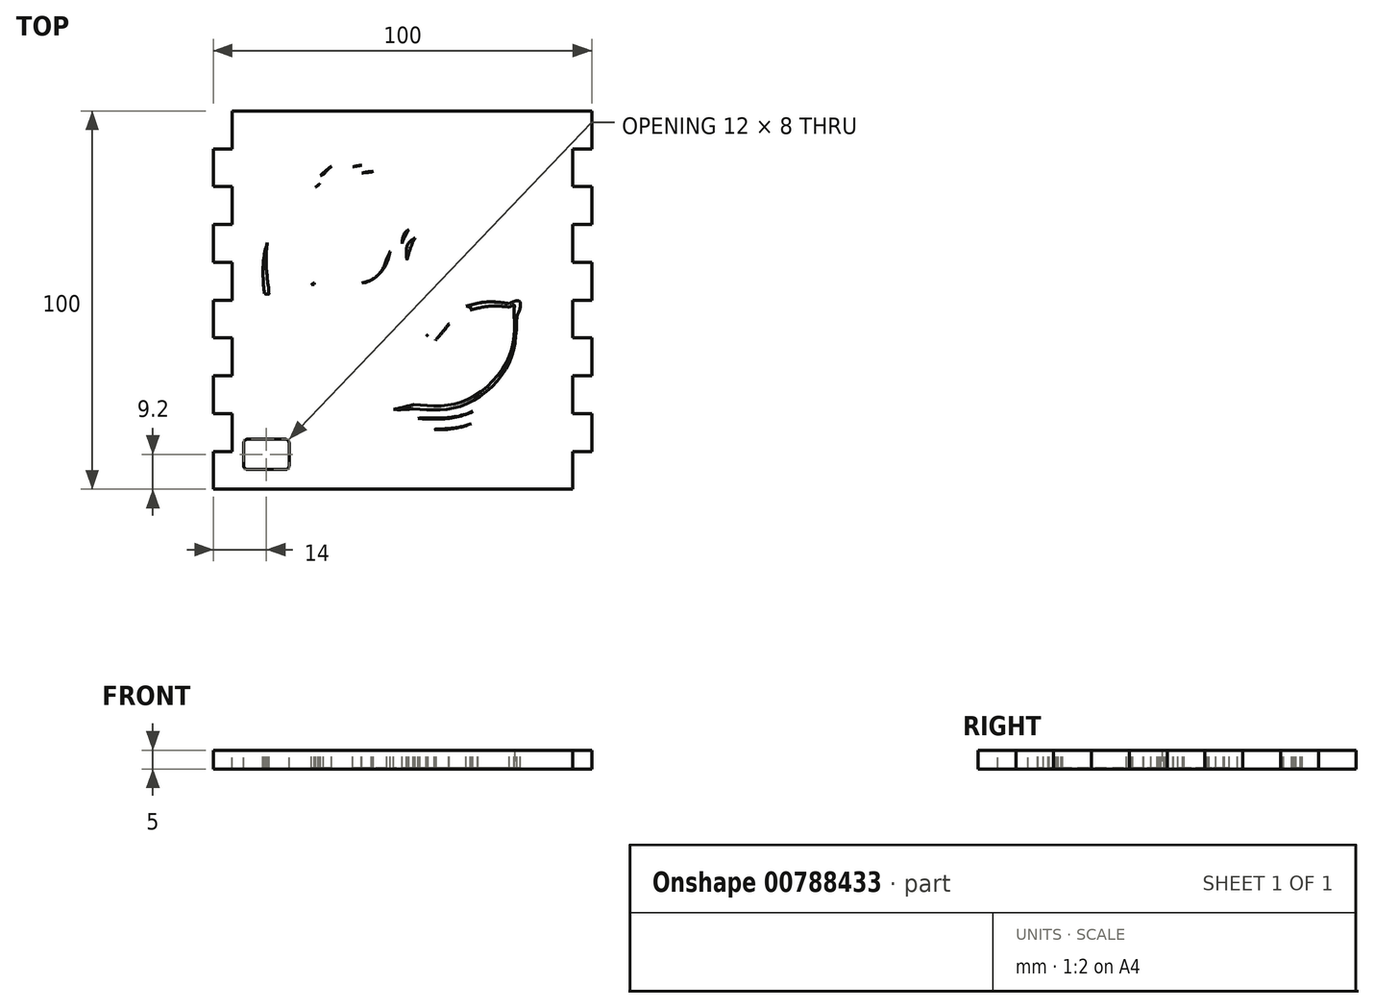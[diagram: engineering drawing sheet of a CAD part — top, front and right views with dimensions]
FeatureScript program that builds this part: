
annotation { "Feature Type Name" : "Feature", "Feature Type Description" : "" }
export const myFeature = defineFeature(function(context is Context, id is Id, definition is map)
    precondition{}
    {
        {
            var Q0;
            Q0=qCreatedBy(makeId("Top.planeOp"),FACE);
            var sketch = newSketch(context, id + "F0", { "sketchPlane" : qUnion([Q0])});
            skLineSegment(sketch, "E0.bottom", {"start": v(50, -50) * mm, "end": v(-50, -50) * mm});
            skLineSegment(sketch, "E0.top", {"start": v(50, 50) * mm, "end": v(-50, 50) * mm});
            skLineSegment(sketch, "E0.left", {"start": v(50, -50) * mm, "end": v(50, 50) * mm});
            skLineSegment(sketch, "E0.right", {"start": v(-50, -50) * mm, "end": v(-50, 50) * mm});
            skPoint(sketch, "E0.middle", {"position": v(0, 0) * mm});
            skSolve(sketch);
        }
        {
            var Q0;
            Q0=qSketchRegion(id+"F0",true);
            extrude(context, id + "F1", {"entities" : qUnion([Q0]), "depth" : 5 * mm, "offsetDistance" : 25 * mm});
        }
        {
            var Q0;
            Q0=makeQuery(id+"F1.opExtrude","CAP_FACE",FACE,{"disambiguationData":[OSD([sQuery(id+"F0.wireOp",EDGE,"E0.bottom"),sQuery(id+"F0.wireOp",EDGE,"E0.top"),sQuery(id+"F0.wireOp",EDGE,"E0.left"),sQuery(id+"F0.wireOp",EDGE,"E0.right")])],"isStart":false});
            var sketch = newSketch(context, id + "F2", { "sketchPlane" : qUnion([Q0])});
            skLineSegment(sketch, "E1.bottom", {"start": v(-50, 50) * mm, "end": v(-45, 50) * mm});
            skLineSegment(sketch, "E1.top", {"start": v(-50, 40) * mm, "end": v(-45, 40) * mm});
            skLineSegment(sketch, "E1.left", {"start": v(-50, 50) * mm, "end": v(-50, 40) * mm});
            skLineSegment(sketch, "E1.right", {"start": v(-45, 50) * mm, "end": v(-45, 40) * mm});
            skLineSegment(sketch, "E2.bottom", {"start": v(-45, 30) * mm, "end": v(-55, 30) * mm});
            skLineSegment(sketch, "E2.top", {"start": v(-45, 20) * mm, "end": v(-55, 20) * mm});
            skLineSegment(sketch, "E2.left", {"start": v(-45, 30) * mm, "end": v(-45, 20) * mm});
            skLineSegment(sketch, "E2.right", {"start": v(-55, 30) * mm, "end": v(-55, 20) * mm});
            skLineSegment(sketch, "E3.bottom", {"start": v(-45, 10) * mm, "end": v(-55, 10) * mm});
            skLineSegment(sketch, "E3.top", {"start": v(-45, 0) * mm, "end": v(-55, 0) * mm});
            skLineSegment(sketch, "E3.left", {"start": v(-45, 10) * mm, "end": v(-45, 0) * mm});
            skLineSegment(sketch, "E3.right", {"start": v(-55, 10) * mm, "end": v(-55, 0) * mm});
            skLineSegment(sketch, "E4.bottom", {"start": v(-45, -10) * mm, "end": v(-55, -10) * mm});
            skLineSegment(sketch, "E4.top", {"start": v(-45, -20) * mm, "end": v(-55, -20) * mm});
            skLineSegment(sketch, "E4.left", {"start": v(-45, -10) * mm, "end": v(-45, -20) * mm});
            skLineSegment(sketch, "E4.right", {"start": v(-55, -10) * mm, "end": v(-55, -20) * mm});
            skLineSegment(sketch, "E5.bottom", {"start": v(-55, -30) * mm, "end": v(-45, -30) * mm});
            skLineSegment(sketch, "E5.top", {"start": v(-55, -40) * mm, "end": v(-45, -40) * mm});
            skLineSegment(sketch, "E5.left", {"start": v(-55, -30) * mm, "end": v(-55, -40) * mm});
            skLineSegment(sketch, "E5.right", {"start": v(-45, -30) * mm, "end": v(-45, -40) * mm});
            skSolve(sketch);
        }
        {
            var Q0;
            Q0=qSketchRegion(id+"F2",true);
            extrude(context, id + "F3", {"entities" : qUnion([Q0]), "operationType" : NewBodyOperationType.REMOVE, "oppositeDirection" : true, "depth" : 5 * mm, "offsetDistance" : 25 * mm});
        }
        {
            var Q0;
            Q0=makeQuery(id+"F1.opExtrude","CAP_FACE",FACE,{"disambiguationData":[OSD([sQuery(id+"F0.wireOp",EDGE,"E0.bottom"),sQuery(id+"F0.wireOp",EDGE,"E0.top"),sQuery(id+"F0.wireOp",EDGE,"E0.left"),sQuery(id+"F0.wireOp",EDGE,"E0.right")])],"isStart":false});
            var sketch = newSketch(context, id + "F4", { "sketchPlane" : qUnion([Q0])});
            skLineSegment(sketch, "E6.bottom", {"start": v(45, -40) * mm, "end": v(50, -40) * mm});
            skLineSegment(sketch, "E6.top", {"start": v(45, -50) * mm, "end": v(50, -50) * mm});
            skLineSegment(sketch, "E6.left", {"start": v(45, -40) * mm, "end": v(45, -50) * mm});
            skLineSegment(sketch, "E6.right", {"start": v(50, -40) * mm, "end": v(50, -50) * mm});
            skLineSegment(sketch, "E7.bottom", {"start": v(45, -20) * mm, "end": v(50, -20) * mm});
            skLineSegment(sketch, "E7.top", {"start": v(45, -30) * mm, "end": v(50, -30) * mm});
            skLineSegment(sketch, "E7.left", {"start": v(45, -20) * mm, "end": v(45, -30) * mm});
            skLineSegment(sketch, "E7.right", {"start": v(50, -20) * mm, "end": v(50, -30) * mm});
            skLineSegment(sketch, "E8.bottom", {"start": v(45, 0) * mm, "end": v(50, 0) * mm});
            skLineSegment(sketch, "E8.top", {"start": v(45, -10) * mm, "end": v(50, -10) * mm});
            skLineSegment(sketch, "E8.left", {"start": v(45, 0) * mm, "end": v(45, -10) * mm});
            skLineSegment(sketch, "E8.right", {"start": v(50, 0) * mm, "end": v(50, -10) * mm});
            skLineSegment(sketch, "E9.bottom", {"start": v(45, 20) * mm, "end": v(50, 20) * mm});
            skLineSegment(sketch, "E9.top", {"start": v(45, 10) * mm, "end": v(50, 10) * mm});
            skLineSegment(sketch, "E9.left", {"start": v(45, 20) * mm, "end": v(45, 10) * mm});
            skLineSegment(sketch, "E9.right", {"start": v(50, 20) * mm, "end": v(50, 10) * mm});
            skLineSegment(sketch, "E10.bottom", {"start": v(45, 40) * mm, "end": v(50, 40) * mm});
            skLineSegment(sketch, "E10.top", {"start": v(45, 30) * mm, "end": v(50, 30) * mm});
            skLineSegment(sketch, "E10.left", {"start": v(45, 40) * mm, "end": v(45, 30) * mm});
            skLineSegment(sketch, "E10.right", {"start": v(50, 40) * mm, "end": v(50, 30) * mm});
            skSolve(sketch);
        }
        {
            var Q0;
            Q0=qSketchRegion(id+"F4",true);
            extrude(context, id + "F5", {"entities" : qUnion([Q0]), "operationType" : NewBodyOperationType.REMOVE, "oppositeDirection" : true, "depth" : 5 * mm, "offsetDistance" : 25 * mm});
        }
        {
            var Q0;
            Q0=makeQuery(id+"F1.opExtrude","CAP_FACE",FACE,{"disambiguationData":[OSD([sQuery(id+"F0.wireOp",EDGE,"E0.bottom"),sQuery(id+"F0.wireOp",EDGE,"E0.top"),sQuery(id+"F0.wireOp",EDGE,"E0.left"),sQuery(id+"F0.wireOp",EDGE,"E0.right")])],"isStart":false});
            var sketch = newSketch(context, id + "F6", { "sketchPlane" : qUnion([Q0])});
            skFitSpline(sketch, "E11", {"points": [v(-1.5, -35.05) * mm, v(-16.6, -34.56) * mm, v(-30.6, -23.77) * mm, v(-34.95, -9.31) * mm]});
            skFitSpline(sketch, "E12", {"points": [v(-34.95, -9.31) * mm, v(-39.38, 4.29) * mm, v(-34.95, 20.21) * mm, v(-24.04, 29.5) * mm]});
            skFitSpline(sketch, "E13", {"points": [v(-24.04, 29.5) * mm, v(-12.77, 39.67) * mm, v(4.96, 41.47) * mm, v(18.1, 33.94) * mm]});
            skFitSpline(sketch, "E14", {"points": [v(18.1, 33.94) * mm, v(30.56, 27.18) * mm, v(38.25, 12.78) * mm, v(36.9, -1.33) * mm]});
            skFitSpline(sketch, "E15", {"points": [v(36.9, -1.33) * mm, v(35.83, -16.44) * mm, v(24.45, -30.09) * mm, v(9.77, -33.82) * mm]});
            skFitSpline(sketch, "E16", {"points": [v(9.77, -33.82) * mm, v(6.1, -34.81) * mm, v(2.28, -35.24) * mm, v(-1.5, -35.05) * mm]});
            skFitSpline(sketch, "E17", {"points": [v(3.11, -34.85) * mm, v(18.23, -33.86) * mm, v(31.88, -22.48) * mm, v(35.63, -7.82) * mm]});
            skFitSpline(sketch, "E18", {"points": [v(35.63, -7.82) * mm, v(36.47, -4.77) * mm, v(36.85, -1.61) * mm, v(36.92, 1.55) * mm]});
            skFitSpline(sketch, "E19", {"points": [v(36.92, 1.55) * mm, v(34.37, 0.85) * mm, v(36.28, -4.46) * mm, v(34.77, -6.8) * mm]});
            skFitSpline(sketch, "E20", {"points": [v(34.77, -6.8) * mm, v(31.4, -21.33) * mm, v(18, -32.73) * mm, v(3.12, -33.75) * mm]});
            skFitSpline(sketch, "E21", {"points": [v(3.12, -33.75) * mm, v(-11.13, -35.13) * mm, v(-25.62, -26.87) * mm, v(-31.78, -13.97) * mm]});
            skFitSpline(sketch, "E22", {"points": [v(-31.78, -13.97) * mm, v(-34.01, -9.49) * mm, v(-35.2, -4.53) * mm, v(-35.42, 0.47) * mm]});
            skFitSpline(sketch, "E23", {"points": [v(-35.42, 0.47) * mm, v(-30.66, 0.48) * mm, v(-25.9, 0.48) * mm, v(-21.15, 0.5) * mm]});
            skFitSpline(sketch, "E24", {"points": [v(-21.15, 0.5) * mm, v(-21.52, 2.1) * mm, v(-23.24, 1.37) * mm, v(-24.46, 1.53) * mm]});
            skFitSpline(sketch, "E25", {"points": [v(-24.46, 1.53) * mm, v(-28.48, 1.53) * mm, v(-32.51, 1.54) * mm, v(-36.54, 1.55) * mm]});
            skFitSpline(sketch, "E26", {"points": [v(-36.54, 1.55) * mm, v(-36.6, -12.8) * mm, v(-27.4, -26.62) * mm, v(-14.12, -32.06) * mm]});
            skFitSpline(sketch, "E27", {"points": [v(-14.12, -32.06) * mm, v(-8.7, -34.37) * mm, v(-2.75, -35.3) * mm, v(3.11, -34.85) * mm]});
            skFitSpline(sketch, "E28", {"points": [v(1.99, -33.7) * mm, v(16.8, -33.17) * mm, v(30.44, -22.27) * mm, v(34.32, -7.98) * mm]});
            skFitSpline(sketch, "E29", {"points": [v(34.32, -7.98) * mm, v(35.22, -4.89) * mm, v(35.63, -1.67) * mm, v(35.7, 1.55) * mm]});
            skFitSpline(sketch, "E30", {"points": [v(35.7, 1.55) * mm, v(33.32, 0.9) * mm, v(34.96, -3.87) * mm, v(33.67, -6.14) * mm]});
            skFitSpline(sketch, "E31", {"points": [v(33.67, -6.14) * mm, v(30.57, -20.12) * mm, v(17.9, -31.27) * mm, v(3.61, -32.48) * mm]});
            skFitSpline(sketch, "E32", {"points": [v(3.61, -32.48) * mm, v(-10.39, -34.09) * mm, v(-24.77, -26.01) * mm, v(-30.76, -13.27) * mm]});
            skFitSpline(sketch, "E33", {"points": [v(-30.76, -13.27) * mm, v(-32.66, -9.36) * mm, v(-33.81, -5.09) * mm, v(-34.11, -0.75) * mm]});
            skFitSpline(sketch, "E34", {"points": [v(-34.11, -0.75) * mm, v(-29.54, -0.74) * mm, v(-24.98, -0.74) * mm, v(-20.4, -0.73) * mm]});
            skFitSpline(sketch, "E35", {"points": [v(-20.4, -0.73) * mm, v(-20.82, 0.86) * mm, v(-22.52, 0.16) * mm, v(-23.75, 0.3) * mm]});
            skFitSpline(sketch, "E36", {"points": [v(-23.75, 0.3) * mm, v(-27.6, 0.31) * mm, v(-31.44, 0.32) * mm, v(-35.28, 0.33) * mm]});
            skFitSpline(sketch, "E37", {"points": [v(-35.28, 0.33) * mm, v(-34.9, -14.29) * mm, v(-24.47, -27.89) * mm, v(-10.48, -32.1) * mm]});
            skFitSpline(sketch, "E38", {"points": [v(-10.48, -32.1) * mm, v(-6.47, -33.38) * mm, v(-2.22, -33.9) * mm, v(1.99, -33.7) * mm]});
            skFitSpline(sketch, "E39", {"points": [v(1.94, -32.48) * mm, v(15.86, -31.96) * mm, v(28.76, -22) * mm, v(32.83, -8.69) * mm]});
            skFitSpline(sketch, "E40", {"points": [v(32.83, -8.69) * mm, v(33.9, -5.38) * mm, v(34.42, -1.92) * mm, v(34.46, 1.55) * mm]});
            skFitSpline(sketch, "E41", {"points": [v(34.46, 1.55) * mm, v(31.93, 1.7) * mm, v(33.96, -2.9) * mm, v(32.78, -4.52) * mm]});
            skFitSpline(sketch, "E42", {"points": [v(32.78, -4.52) * mm, v(30.31, -18.23) * mm, v(18.38, -29.53) * mm, v(4.53, -31.14) * mm]});
            skFitSpline(sketch, "E43", {"points": [v(4.53, -31.14) * mm, v(-8.56, -33.06) * mm, v(-22.3, -26.17) * mm, v(-28.68, -14.6) * mm]});
            skFitSpline(sketch, "E44", {"points": [v(-28.68, -14.6) * mm, v(-30.89, -10.73) * mm, v(-32.28, -6.41) * mm, v(-32.79, -2) * mm]});
            skFitSpline(sketch, "E45", {"points": [v(-32.79, -2) * mm, v(-28.4, -1.95) * mm, v(-24, -1.96) * mm, v(-19.62, -1.95) * mm]});
            skFitSpline(sketch, "E46", {"points": [v(-19.62, -1.95) * mm, v(-20, -0.5) * mm, v(-21.43, -0.93) * mm, v(-22.6, -0.9) * mm]});
            skFitSpline(sketch, "E47", {"points": [v(-22.6, -0.9) * mm, v(-26.4, -0.9) * mm, v(-30.2, -0.9) * mm, v(-33.99, -0.9) * mm]});
            skFitSpline(sketch, "E48", {"points": [v(-33.99, -0.9) * mm, v(-33.08, -14.98) * mm, v(-22.54, -27.74) * mm, v(-8.88, -31.3) * mm]});
            skFitSpline(sketch, "E49", {"points": [v(-8.88, -31.3) * mm, v(-5.37, -32.27) * mm, v(-1.7, -32.65) * mm, v(1.94, -32.48) * mm]});
            skFitSpline(sketch, "E50", {"points": [v(2.93, -31.19) * mm, v(16.67, -30.25) * mm, v(29.04, -19.74) * mm, v(32.23, -6.35) * mm]});
            skFitSpline(sketch, "E51", {"points": [v(32.23, -6.35) * mm, v(32.9, -3.77) * mm, v(33.2, -1.11) * mm, v(33.25, 1.55) * mm]});
            skFitSpline(sketch, "E52", {"points": [v(33.25, 1.55) * mm, v(26.5, 1.68) * mm, v(19.7, 1.12) * mm, v(13, 2.13) * mm]});
            skFitSpline(sketch, "E53", {"points": [v(13, 2.13) * mm, v(8.36, 2.87) * mm, v(4.32, 5.96) * mm, v(2.22, 10.13) * mm]});
            skFitSpline(sketch, "E54", {"points": [v(2.22, 10.13) * mm, v(1.4, 6.17) * mm, v(6.94, 2.99) * mm, v(10.39, 1.69) * mm]});
            skFitSpline(sketch, "E55", {"points": [v(10.39, 1.69) * mm, v(16.73, -0.21) * mm, v(23.42, 0.69) * mm, v(29.95, 0.47) * mm]});
            skFitSpline(sketch, "E56", {"points": [v(29.95, 0.47) * mm, v(33.12, 1.41) * mm, v(32.02, -1.75) * mm, v(31.65, -3.85) * mm]});
            skFitSpline(sketch, "E57", {"points": [v(31.65, -3.85) * mm, v(29.45, -17.51) * mm, v(17.4, -28.76) * mm, v(3.63, -30.02) * mm]});
            skFitSpline(sketch, "E58", {"points": [v(3.63, -30.02) * mm, v(-9.54, -31.64) * mm, v(-23.17, -24.02) * mm, v(-28.68, -11.94) * mm]});
            skFitSpline(sketch, "E59", {"points": [v(-28.68, -11.94) * mm, v(-30.7, -9.2) * mm, v(-30.39, -4.2) * mm, v(-32.1, -2.11) * mm]});
            skFitSpline(sketch, "E60", {"points": [v(-32.1, -2.11) * mm, v(-33.32, -4.07) * mm, v(-30.97, -8.8) * mm, v(-30.11, -11.46) * mm]});
            skFitSpline(sketch, "E61", {"points": [v(-30.11, -11.46) * mm, v(-24.71, -24.22) * mm, v(-10.89, -32.5) * mm, v(2.93, -31.19) * mm]});
            skFitSpline(sketch, "E62", {"points": [v(1.8, -30.03) * mm, v(15.26, -29.56) * mm, v(27.63, -19.54) * mm, v(30.94, -6.49) * mm]});
            skFitSpline(sketch, "E63", {"points": [v(30.94, -6.49) * mm, v(30.84, -4.7) * mm, v(33.53, 0.22) * mm, v(30.95, 0.32) * mm]});
            skFitSpline(sketch, "E64", {"points": [v(30.95, 0.32) * mm, v(24.5, 0.51) * mm, v(17.97, -0.2) * mm, v(11.63, 1.19) * mm]});
            skFitSpline(sketch, "E65", {"points": [v(11.63, 1.19) * mm, v(7.38, 2.14) * mm, v(3.78, 5.04) * mm, v(1.56, 8.74) * mm]});
            skFitSpline(sketch, "E66", {"points": [v(1.56, 8.74) * mm, v(0.56, 5.95) * mm, v(4.6, 3.6) * mm, v(6.7, 2.01) * mm]});
            skFitSpline(sketch, "E67", {"points": [v(6.7, 2.01) * mm, v(13.32, -1.76) * mm, v(21.17, -0.5) * mm, v(28.46, -0.75) * mm]});
            skFitSpline(sketch, "E68", {"points": [v(28.46, -0.75) * mm, v(31, -0.1) * mm, v(31.25, -1.65) * mm, v(30.4, -3.9) * mm]});
            skFitSpline(sketch, "E69", {"points": [v(30.4, -3.9) * mm, v(28.11, -17.42) * mm, v(15.8, -28.33) * mm, v(2.1, -28.92) * mm]});
            skFitSpline(sketch, "E70", {"points": [v(2.1, -28.92) * mm, v(-11.15, -29.95) * mm, v(-24.37, -21.3) * mm, v(-28.71, -8.74) * mm]});
            skFitSpline(sketch, "E71", {"points": [v(-28.71, -8.74) * mm, v(-30.23, -7.25) * mm, v(-28.96, -1.48) * mm, v(-31.4, -2.27) * mm]});
            skFitSpline(sketch, "E72", {"points": [v(-31.4, -2.27) * mm, v(-29.89, -15.47) * mm, v(-19.25, -26.96) * mm, v(-6.19, -29.43) * mm]});
            skFitSpline(sketch, "E73", {"points": [v(-6.19, -29.43) * mm, v(-3.57, -29.97) * mm, v(-0.87, -30.18) * mm, v(1.8, -30.03) * mm]});
            skFitSpline(sketch, "E74", {"points": [v(2.83, -28.75) * mm, v(16.07, -27.8) * mm, v(27.83, -17.26) * mm, v(30.21, -4.21) * mm]});
            skFitSpline(sketch, "E75", {"points": [v(30.21, -4.21) * mm, v(31.14, -1.82) * mm, v(30.83, -0.24) * mm, v(28.17, -0.9) * mm]});
            skFitSpline(sketch, "E76", {"points": [v(28.17, -0.9) * mm, v(20.7, -0.66) * mm, v(12.58, -1.92) * mm, v(5.96, 2.32) * mm]});
            skFitSpline(sketch, "E77", {"points": [v(5.96, 2.32) * mm, v(3.8, 3.18) * mm, v(2.04, 6.74) * mm, v(0.7, 7.24) * mm]});
            skFitSpline(sketch, "E78", {"points": [v(0.7, 7.24) * mm, v(0, 4.46) * mm, v(4.79, 2.06) * mm, v(6.83, 0.55) * mm]});
            skFitSpline(sketch, "E79", {"points": [v(6.83, 0.55) * mm, v(13.85, -2.97) * mm, v(21.86, -1.75) * mm, v(29.44, -1.97) * mm]});
            skFitSpline(sketch, "E80", {"points": [v(29.44, -1.97) * mm, v(28.04, -15.33) * mm, v(16.32, -26.65) * mm, v(2.92, -27.64) * mm]});
            skFitSpline(sketch, "E81", {"points": [v(2.92, -27.64) * mm, v(-9.73, -29.02) * mm, v(-22.62, -21.13) * mm, v(-27.2, -9.26) * mm]});
            skFitSpline(sketch, "E82", {"points": [v(-27.2, -9.26) * mm, v(-28.51, -7.6) * mm, v(-28.38, -1.31) * mm, v(-30.12, -2.55) * mm]});
            skFitSpline(sketch, "E83", {"points": [v(-30.12, -2.55) * mm, v(-28.49, -15.41) * mm, v(-17.8, -26.42) * mm, v(-4.98, -28.42) * mm]});
            skFitSpline(sketch, "E84", {"points": [v(-4.98, -28.42) * mm, v(-2.4, -28.88) * mm, v(0.22, -28.93) * mm, v(2.83, -28.75) * mm]});
            skFitSpline(sketch, "E85", {"points": [v(2.74, -27.53) * mm, v(15.84, -26.6) * mm, v(27.4, -15.85) * mm, v(29.22, -2.83) * mm]});
            skFitSpline(sketch, "E86", {"points": [v(29.22, -2.83) * mm, v(29.53, -1.36) * mm, v(26.82, -2.45) * mm, v(25.8, -2.11) * mm]});
            skFitSpline(sketch, "E87", {"points": [v(25.8, -2.11) * mm, v(23.82, -2.11) * mm, v(21.85, -2.11) * mm, v(19.89, -2.11) * mm]});
            skFitSpline(sketch, "E88", {"points": [v(19.89, -2.11) * mm, v(14.22, -10.41) * mm, v(7.3, -17.76) * mm, v(0.17, -24.81) * mm]});
            skFitSpline(sketch, "E89", {"points": [v(0.17, -24.81) * mm, v(-6.95, -17.76) * mm, v(-13.85, -10.4) * mm, v(-19.52, -2.11) * mm]});
            skFitSpline(sketch, "E90", {"points": [v(-19.52, -2.11) * mm, v(-22.66, -2.15) * mm, v(-25.8, -2.03) * mm, v(-28.94, -2.2) * mm]});
            skFitSpline(sketch, "E91", {"points": [v(-28.94, -2.2) * mm, v(-27.41, -14.94) * mm, v(-16.6, -25.81) * mm, v(-3.85, -27.36) * mm]});
            skFitSpline(sketch, "E92", {"points": [v(-3.85, -27.36) * mm, v(-1.67, -27.69) * mm, v(0.54, -27.67) * mm, v(2.74, -27.53) * mm]});
            skFitSpline(sketch, "E93", {"points": [v(2.16, -22.65) * mm, v(8.51, -16.27) * mm, v(14.61, -9.56) * mm, v(19.73, -2.12) * mm]});
            skFitSpline(sketch, "E94", {"points": [v(19.73, -2.12) * mm, v(17.02, -2.08) * mm, v(16.34, -5.94) * mm, v(14.4, -7.5) * mm]});
            skFitSpline(sketch, "E95", {"points": [v(14.4, -7.5) * mm, v(9.99, -13) * mm, v(5.16, -18.15) * mm, v(0.16, -23.11) * mm]});
            skFitSpline(sketch, "E96", {"points": [v(0.16, -23.11) * mm, v(-7.9, -14.85) * mm, v(-16.14, -6.42) * mm, v(-21.58, 3.87) * mm]});
            skFitSpline(sketch, "E97", {"points": [v(-21.58, 3.87) * mm, v(-25.9, 11.84) * mm, v(-19.67, 22.3) * mm, v(-11.03, 23.6) * mm]});
            skFitSpline(sketch, "E98", {"points": [v(-11.03, 23.6) * mm, v(-7.25, 24.28) * mm, v(-3.29, 22.83) * mm, v(-0.65, 20.08) * mm]});
            skFitSpline(sketch, "E99", {"points": [v(-0.65, 20.08) * mm, v(0.72, 22.26) * mm, v(-4.23, 23.8) * mm, v(-6.06, 24.47) * mm]});
            skFitSpline(sketch, "E100", {"points": [v(-6.06, 24.47) * mm, v(-15.9, 27) * mm, v(-25.96, 16.75) * mm, v(-23.8, 6.95) * mm]});
            skFitSpline(sketch, "E101", {"points": [v(-23.8, 6.95) * mm, v(-22.04, 0.56) * mm, v(-17.6, -4.64) * mm, v(-13.6, -9.77) * mm]});
            skFitSpline(sketch, "E102", {"points": [v(-13.6, -9.77) * mm, v(-9.3, -14.99) * mm, v(-4.65, -19.9) * mm, v(0.16, -24.64) * mm]});
            skFitSpline(sketch, "E103", {"points": [v(0.16, -24.64) * mm, v(0.84, -23.99) * mm, v(1.5, -23.32) * mm, v(2.16, -22.65) * mm]});
            skFitSpline(sketch, "E104", {"points": [v(1.92, -21.15) * mm, v(7.82, -15.2) * mm, v(13.46, -8.96) * mm, v(18.26, -2.09) * mm]});
            skFitSpline(sketch, "E105", {"points": [v(18.26, -2.09) * mm, v(15.47, -1.69) * mm, v(14.94, -6.02) * mm, v(12.91, -7.39) * mm]});
            skFitSpline(sketch, "E106", {"points": [v(12.91, -7.39) * mm, v(8.93, -12.3) * mm, v(4.63, -16.93) * mm, v(0.16, -21.38) * mm]});
            skFitSpline(sketch, "E107", {"points": [v(0.16, -21.38) * mm, v(-7.46, -13.55) * mm, v(-15.16, -5.5) * mm, v(-20.38, 4.19) * mm]});
            skFitSpline(sketch, "E108", {"points": [v(-20.38, 4.19) * mm, v(-24.4, 11.3) * mm, v(-19.1, 20.73) * mm, v(-11.42, 22.29) * mm]});
            skFitSpline(sketch, "E109", {"points": [v(-11.42, 22.29) * mm, v(-7.64, 23.75) * mm, v(-3.54, 20.52) * mm, v(-1.07, 19.57) * mm]});
            skFitSpline(sketch, "E110", {"points": [v(-1.07, 19.57) * mm, v(-1.43, 22.24) * mm, v(-6.84, 23.8) * mm, v(-9.66, 23.62) * mm]});
            skFitSpline(sketch, "E111", {"points": [v(-9.66, 23.62) * mm, v(-18.56, 23.27) * mm, v(-25.63, 12.93) * mm, v(-21.8, 4.64) * mm]});
            skFitSpline(sketch, "E112", {"points": [v(-21.8, 4.64) * mm, v(-17.22, -4.66) * mm, v(-10, -12.3) * mm, v(-2.95, -19.77) * mm]});
            skFitSpline(sketch, "E113", {"points": [v(-2.95, -19.77) * mm, v(-1.13, -21.16) * mm, v(0.03, -24.64) * mm, v(1.92, -21.15) * mm]});
            skFitSpline(sketch, "E114", {"points": [v(1.73, -19.6) * mm, v(7.15, -14.1) * mm, v(12.32, -8.33) * mm, v(16.82, -2.04) * mm]});
            skFitSpline(sketch, "E115", {"points": [v(16.82, -2.04) * mm, v(14.41, -1.4) * mm, v(13.95, -5.13) * mm, v(12.27, -6.25) * mm]});
            skFitSpline(sketch, "E116", {"points": [v(12.27, -6.25) * mm, v(8.48, -10.93) * mm, v(4.42, -15.39) * mm, v(0.16, -19.64) * mm]});
            skFitSpline(sketch, "E117", {"points": [v(0.16, -19.64) * mm, v(-7.1, -12.08) * mm, v(-14.52, -4.35) * mm, v(-19.42, 5.01) * mm]});
            skFitSpline(sketch, "E118", {"points": [v(-19.42, 5.01) * mm, v(-23.53, 12.64) * mm, v(-15.69, 22.8) * mm, v(-7.32, 21.13) * mm]});
            skFitSpline(sketch, "E119", {"points": [v(-7.32, 21.13) * mm, v(-5.03, 21.78) * mm, v(-2.8, 16.92) * mm, v(-1.54, 18.96) * mm]});
            skFitSpline(sketch, "E120", {"points": [v(-1.54, 18.96) * mm, v(-5.08, 23.31) * mm, v(-12.11, 23.4) * mm, v(-16.3, 19.85) * mm]});
            skFitSpline(sketch, "E121", {"points": [v(-16.3, 19.85) * mm, v(-21.18, 16.37) * mm, v(-23.24, 9.23) * mm, v(-20.11, 3.94) * mm]});
            skFitSpline(sketch, "E122", {"points": [v(-20.11, 3.94) * mm, v(-14.92, -5.55) * mm, v(-7.37, -13.5) * mm, v(0.16, -21.17) * mm]});
            skFitSpline(sketch, "E123", {"points": [v(0.16, -21.17) * mm, v(0.7, -20.66) * mm, v(1.21, -20.13) * mm, v(1.73, -19.6) * mm]});
            skFitSpline(sketch, "E124", {"points": [v(0.61, -19.02) * mm, v(5.9, -13.64) * mm, v(10.98, -8.02) * mm, v(15.42, -1.9) * mm]});
            skFitSpline(sketch, "E125", {"points": [v(15.42, -1.9) * mm, v(12.25, -2.14) * mm, v(11.1, -6.89) * mm, v(8.58, -8.77) * mm]});
            skFitSpline(sketch, "E126", {"points": [v(8.58, -8.77) * mm, v(5.88, -11.92) * mm, v(3.08, -14.97) * mm, v(0.16, -17.9) * mm]});
            skFitSpline(sketch, "E127", {"points": [v(0.16, -17.9) * mm, v(-6.77, -10.6) * mm, v(-13.87, -3.15) * mm, v(-18.48, 5.89) * mm]});
            skFitSpline(sketch, "E128", {"points": [v(-18.48, 5.89) * mm, v(-22.04, 13.1) * mm, v(-13.75, 22.5) * mm, v(-6.19, 19.52) * mm]});
            skFitSpline(sketch, "E129", {"points": [v(-6.19, 19.52) * mm, v(-5.06, 18.98) * mm, v(-1.4, 15.97) * mm, v(-2.67, 18.46) * mm]});
            skFitSpline(sketch, "E130", {"points": [v(-2.67, 18.46) * mm, v(-6.59, 22.67) * mm, v(-13.58, 21.6) * mm, v(-17.13, 17.48) * mm]});
            skFitSpline(sketch, "E131", {"points": [v(-17.13, 17.48) * mm, v(-20.72, 13.94) * mm, v(-21.46, 8) * mm, v(-18.65, 3.78) * mm]});
            skFitSpline(sketch, "E132", {"points": [v(-18.65, 3.78) * mm, v(-13.66, -4.9) * mm, v(-6.81, -12.33) * mm, v(0.17, -19.43) * mm]});
            skFitSpline(sketch, "E133", {"points": [v(1.28, -16.59) * mm, v(5.8, -11.9) * mm, v(10.15, -7.03) * mm, v(14, -1.77) * mm]});
            skFitSpline(sketch, "E134", {"points": [v(14, -1.77) * mm, v(10.78, -2.1) * mm, v(9.34, -7.1) * mm, v(6.66, -9.14) * mm]});
            skFitSpline(sketch, "E135", {"points": [v(6.66, -9.14) * mm, v(4.56, -11.54) * mm, v(2.39, -13.89) * mm, v(0.16, -16.17) * mm]});
            skFitSpline(sketch, "E136", {"points": [v(0.16, -16.17) * mm, v(-6.35, -9.17) * mm, v(-13.12, -2.09) * mm, v(-17.44, 6.53) * mm]});
            skFitSpline(sketch, "E137", {"points": [v(-17.44, 6.53) * mm, v(-20.53, 13.06) * mm, v(-12.47, 21.54) * mm, v(-5.91, 18.03) * mm]});
            skFitSpline(sketch, "E138", {"points": [v(-5.91, 18.03) * mm, v(-4.91, 17) * mm, v(-1.97, 15.05) * mm, v(-3.47, 17.53) * mm]});
            skFitSpline(sketch, "E139", {"points": [v(-3.47, 17.53) * mm, v(-6.87, 21.28) * mm, v(-13.08, 20.33) * mm, v(-16.2, 16.7) * mm]});
            skFitSpline(sketch, "E140", {"points": [v(-16.2, 16.7) * mm, v(-19.62, 13.4) * mm, v(-20.14, 7.78) * mm, v(-17.33, 3.92) * mm]});
            skFitSpline(sketch, "E141", {"points": [v(-17.33, 3.92) * mm, v(-12.63, -4.14) * mm, v(-6.24, -11.04) * mm, v(0.18, -17.75) * mm]});
            skFitSpline(sketch, "E142", {"points": [v(0.18, -17.75) * mm, v(0.54, -17.36) * mm, v(0.91, -16.97) * mm, v(1.28, -16.59) * mm]});
            skLineSegment(sketch, "E143", {"start": v(0.17, -19.43) * mm, "end": v(0.61, -19.02) * mm});
            skLineSegment(sketch, "E144", {"start": v(0.61, -19.02) * mm, "end": v(0.17, -19.43) * mm});
            skFitSpline(sketch, "E145", {"points": [v(0.75, -15.38) * mm, v(4.95, -10.98) * mm, v(9.03, -6.44) * mm, v(12.64, -1.54) * mm]});
            skFitSpline(sketch, "E146", {"points": [v(12.64, -1.54) * mm, v(9.51, -1.7) * mm, v(8.12, -6.55) * mm, v(5.56, -8.53) * mm]});
            skFitSpline(sketch, "E147", {"points": [v(5.56, -8.53) * mm, v(3.69, -9.93) * mm, v(1.74, -14.1) * mm, v(-0.22, -14) * mm]});
            skFitSpline(sketch, "E148", {"points": [v(-0.22, -14) * mm, v(-6.21, -7.48) * mm, v(-12.41, -0.87) * mm, v(-16.36, 7.15) * mm]});
            skFitSpline(sketch, "E149", {"points": [v(-16.36, 7.15) * mm, v(-18.88, 12.78) * mm, v(-11.74, 20.11) * mm, v(-6.2, 16.78) * mm]});
            skFitSpline(sketch, "E150", {"points": [v(-6.2, 16.78) * mm, v(-5.17, 15.56) * mm, v(-2.75, 13.56) * mm, v(-4.08, 16.4) * mm]});
            skFitSpline(sketch, "E151", {"points": [v(-4.08, 16.4) * mm, v(-6.79, 19.71) * mm, v(-11.97, 19.25) * mm, v(-14.8, 16.36) * mm]});
            skFitSpline(sketch, "E152", {"points": [v(-14.8, 16.36) * mm, v(-18.08, 13.59) * mm, v(-19, 8.48) * mm, v(-16.48, 4.9) * mm]});
            skFitSpline(sketch, "E153", {"points": [v(-16.48, 4.9) * mm, v(-12.05, -2.86) * mm, v(-5.97, -9.51) * mm, v(0.16, -15.96) * mm]});
            skFitSpline(sketch, "E154", {"points": [v(0.44, -13.95) * mm, v(4.25, -9.9) * mm, v(8, -5.75) * mm, v(11.3, -1.27) * mm]});
            skFitSpline(sketch, "E155", {"points": [v(11.3, -1.27) * mm, v(6.77, -0.25) * mm, v(2.75, 2.55) * mm, v(0.18, 6.4) * mm]});
            skFitSpline(sketch, "E156", {"points": [v(0.18, 6.4) * mm, v(-2.35, 2.53) * mm, v(-6.4, -0.24) * mm, v(-10.9, -1.25) * mm]});
            skFitSpline(sketch, "E157", {"points": [v(-10.9, -1.25) * mm, v(-7.59, -5.86) * mm, v(-3.72, -10.08) * mm, v(0.16, -14.22) * mm]});
            skLineSegment(sketch, "E158", {"start": v(0.16, -15.96) * mm, "end": v(0.75, -15.38) * mm});
            skLineSegment(sketch, "E159", {"start": v(0.75, -15.38) * mm, "end": v(0.16, -15.96) * mm});
            skFitSpline(sketch, "E160", {"points": [v(-10.33, -0.96) * mm, v(-3.97, 0.55) * mm, v(0.71, 5.9) * mm, v(2.82, 11.9) * mm]});
            skFitSpline(sketch, "E161", {"points": [v(2.82, 11.9) * mm, v(4.14, 15.12) * mm, v(7.18, 18.58) * mm, v(11.04, 17.46) * mm]});
            skFitSpline(sketch, "E162", {"points": [v(11.04, 17.46) * mm, v(15.6, 16.26) * mm, v(18.9, 10.57) * mm, v(16.32, 6.23) * mm]});
            skFitSpline(sketch, "E163", {"points": [v(16.32, 6.23) * mm, v(17, 3.58) * mm, v(19, 9.11) * mm, v(18.27, 10.6) * mm]});
            skFitSpline(sketch, "E164", {"points": [v(18.27, 10.6) * mm, v(17.71, 16.1) * mm, v(10.85, 21.04) * mm, v(5.82, 17.58) * mm]});
            skFitSpline(sketch, "E165", {"points": [v(5.82, 17.58) * mm, v(1.2, 14.26) * mm, v(1.07, 7.7) * mm, v(-3.33, 4.12) * mm]});
            skFitSpline(sketch, "E166", {"points": [v(-3.33, 4.12) * mm, v(-5.13, 1.49) * mm, v(-10.25, 0.84) * mm, v(-11.42, -0.68) * mm]});
            skLineSegment(sketch, "E167", {"start": v(0.16, -14.22) * mm, "end": v(0.44, -13.95) * mm});
            skLineSegment(sketch, "E168", {"start": v(0.44, -13.95) * mm, "end": v(0.16, -14.22) * mm});
            skFitSpline(sketch, "E169", {"points": [v(-10.5, 0.26) * mm, v(-4.58, 1.69) * mm, v(-0.35, 6.71) * mm, v(1.65, 12.25) * mm]});
            skFitSpline(sketch, "E170", {"points": [v(1.65, 12.25) * mm, v(3.1, 16.1) * mm, v(6.93, 19.98) * mm, v(11.37, 18.62) * mm]});
            skFitSpline(sketch, "E171", {"points": [v(11.37, 18.62) * mm, v(16.51, 17.3) * mm, v(20.21, 11) * mm, v(17.6, 6.06) * mm]});
            skFitSpline(sketch, "E172", {"points": [v(17.6, 6.06) * mm, v(18.44, 3.58) * mm, v(20.05, 8.9) * mm, v(19.53, 10.31) * mm]});
            skFitSpline(sketch, "E173", {"points": [v(19.53, 10.31) * mm, v(19.17, 16.57) * mm, v(11.8, 22.21) * mm, v(5.87, 19.04) * mm]});
            skFitSpline(sketch, "E174", {"points": [v(5.87, 19.04) * mm, v(0.33, 16.02) * mm, v(0.33, 8.64) * mm, v(-4.38, 4.81) * mm]});
            skFitSpline(sketch, "E175", {"points": [v(-4.38, 4.81) * mm, v(-6.6, 2.7) * mm, v(-9.52, 1.5) * mm, v(-12.48, 0.89) * mm]});
            skFitSpline(sketch, "E176", {"points": [v(-12.48, 0.89) * mm, v(-12.07, -0.32) * mm, v(-11.5, -0.08) * mm, v(-10.5, 0.26) * mm]});
            skLineSegment(sketch, "E177", {"start": v(-11.42, -0.68) * mm, "end": v(-11.01, -1.13) * mm});
            skLineSegment(sketch, "E178", {"start": v(-11.01, -1.13) * mm, "end": v(-10.33, -0.96) * mm});
            skLineSegment(sketch, "E179", {"start": v(-10.33, -0.96) * mm, "end": v(-11.42, -0.68) * mm});
            skFitSpline(sketch, "E180", {"points": [v(-11.85, 1.17) * mm, v(-6.05, 2.23) * mm, v(-1.58, 6.89) * mm, v(0.34, 12.32) * mm]});
            skFitSpline(sketch, "E181", {"points": [v(0.34, 12.32) * mm, v(1.95, 16.68) * mm, v(6.04, 21.06) * mm, v(11.12, 19.94) * mm]});
            skFitSpline(sketch, "E182", {"points": [v(11.12, 19.94) * mm, v(17.32, 18.74) * mm, v(21.8, 11.21) * mm, v(18.65, 5.4) * mm]});
            skFitSpline(sketch, "E183", {"points": [v(18.65, 5.4) * mm, v(21.9, 5.43) * mm, v(20.8, 11.38) * mm, v(20, 13.6) * mm]});
            skFitSpline(sketch, "E184", {"points": [v(20, 13.6) * mm, v(17.86, 19.27) * mm, v(10.6, 23.32) * mm, v(5, 19.96) * mm]});
            skFitSpline(sketch, "E185", {"points": [v(5, 19.96) * mm, v(0.4, 17.42) * mm, v(-0.46, 11.84) * mm, v(-3.28, 7.87) * mm]});
            skFitSpline(sketch, "E186", {"points": [v(-3.28, 7.87) * mm, v(-5.1, 4.13) * mm, v(-10.9, 3) * mm, v(-12.96, 1.5) * mm]});
            skFitSpline(sketch, "E187", {"points": [v(-35.4, 2.87) * mm, v(-35.18, 17.51) * mm, v(-24.84, 31.24) * mm, v(-10.88, 35.61) * mm]});
            skFitSpline(sketch, "E188", {"points": [v(-10.88, 35.61) * mm, v(2.18, 40.02) * mm, v(17.59, 35.95) * mm, v(26.68, 25.55) * mm]});
            skFitSpline(sketch, "E189", {"points": [v(26.68, 25.55) * mm, v(32.3, 19.36) * mm, v(35.58, 11.12) * mm, v(35.8, 2.76) * mm]});
            skFitSpline(sketch, "E190", {"points": [v(35.8, 2.76) * mm, v(28.62, 2.9) * mm, v(21.42, 2.47) * mm, v(14.28, 3.15) * mm]});
            skFitSpline(sketch, "E191", {"points": [v(14.28, 3.15) * mm, v(9.28, 3.63) * mm, v(4.86, 6.93) * mm, v(2.88, 11.52) * mm]});
            skFitSpline(sketch, "E192", {"points": [v(2.88, 11.52) * mm, v(1.3, 9.41) * mm, v(4.71, 7.1) * mm, v(5.99, 5.52) * mm]});
            skFitSpline(sketch, "E193", {"points": [v(5.99, 5.52) * mm, v(11.51, 0.78) * mm, v(19.23, 1.86) * mm, v(25.96, 1.7) * mm]});
            skFitSpline(sketch, "E194", {"points": [v(25.96, 1.7) * mm, v(29.61, 1.7) * mm, v(33.27, 1.7) * mm, v(36.92, 1.68) * mm]});
            skFitSpline(sketch, "E195", {"points": [v(36.92, 1.68) * mm, v(37.07, 15.61) * mm, v(28.53, 29.12) * mm, v(15.87, 34.95) * mm]});
            skFitSpline(sketch, "E196", {"points": [v(15.87, 34.95) * mm, v(2.74, 41.35) * mm, v(-14.07, 38.8) * mm, v(-24.68, 28.75) * mm]});
            skFitSpline(sketch, "E197", {"points": [v(-24.68, 28.75) * mm, v(-32.2, 21.9) * mm, v(-36.58, 11.84) * mm, v(-36.54, 1.69) * mm]});
            skFitSpline(sketch, "E198", {"points": [v(-36.54, 1.69) * mm, v(-35.36, 1.57) * mm, v(-35.34, 1.66) * mm, v(-35.4, 2.87) * mm]});
            skLineSegment(sketch, "E199", {"start": v(-12.96, 1.5) * mm, "end": v(-12.56, 1.03) * mm});
            skLineSegment(sketch, "E200", {"start": v(-12.56, 1.03) * mm, "end": v(-11.85, 1.17) * mm});
            skLineSegment(sketch, "E201", {"start": v(-11.85, 1.17) * mm, "end": v(-12.96, 1.5) * mm});
            skFitSpline(sketch, "E202", {"points": [v(-34.18, 2.85) * mm, v(-33.97, 17.2) * mm, v(-23.68, 30.6) * mm, v(-9.93, 34.63) * mm]});
            skFitSpline(sketch, "E203", {"points": [v(-9.93, 34.63) * mm, v(2.86, 38.72) * mm, v(17.77, 34.42) * mm, v(26.36, 24.07) * mm]});
            skFitSpline(sketch, "E204", {"points": [v(26.36, 24.07) * mm, v(31.15, 18.48) * mm, v(34.06, 11.33) * mm, v(34.5, 3.98) * mm]});
            skFitSpline(sketch, "E205", {"points": [v(34.5, 3.98) * mm, v(27.95, 4.1) * mm, v(21.37, 3.75) * mm, v(14.83, 4.3) * mm]});
            skFitSpline(sketch, "E206", {"points": [v(14.83, 4.3) * mm, v(9.84, 4.64) * mm, v(5.46, 8.04) * mm, v(3.72, 12.68) * mm]});
            skFitSpline(sketch, "E207", {"points": [v(3.72, 12.68) * mm, v(1.66, 12.02) * mm, v(5.14, 8) * mm, v(6.47, 6.72) * mm]});
            skFitSpline(sketch, "E208", {"points": [v(6.47, 6.72) * mm, v(11.8, 1.9) * mm, v(19.41, 3.12) * mm, v(26, 2.92) * mm]});
            skFitSpline(sketch, "E209", {"points": [v(26, 2.92) * mm, v(29.22, 2.92) * mm, v(32.43, 2.91) * mm, v(35.64, 2.9) * mm]});
            skFitSpline(sketch, "E210", {"points": [v(35.64, 2.9) * mm, v(35.44, 17.99) * mm, v(24.37, 32) * mm, v(9.84, 35.9) * mm]});
            skFitSpline(sketch, "E211", {"points": [v(9.84, 35.9) * mm, v(-3.93, 40) * mm, v(-19.82, 34.6) * mm, v(-28.25, 22.97) * mm]});
            skFitSpline(sketch, "E212", {"points": [v(-28.25, 22.97) * mm, v(-32.85, 16.9) * mm, v(-35.3, 9.3) * mm, v(-35.33, 1.69) * mm]});
            skFitSpline(sketch, "E213", {"points": [v(-35.33, 1.69) * mm, v(-34.23, 1.55) * mm, v(-34.07, 1.7) * mm, v(-34.18, 2.85) * mm]});
            skFitSpline(sketch, "E214", {"points": [v(-32.96, 2.83) * mm, v(-32.76, 17.16) * mm, v(-22.08, 30.45) * mm, v(-8.18, 33.86) * mm]});
            skFitSpline(sketch, "E215", {"points": [v(-8.18, 33.86) * mm, v(4.05, 37.18) * mm, v(17.9, 32.7) * mm, v(25.82, 22.81) * mm]});
            skFitSpline(sketch, "E216", {"points": [v(25.82, 22.81) * mm, v(29.93, 17.83) * mm, v(32.53, 11.63) * mm, v(33.2, 5.2) * mm]});
            skFitSpline(sketch, "E217", {"points": [v(33.2, 5.2) * mm, v(26.84, 5.34) * mm, v(20.44, 4.89) * mm, v(14.12, 5.64) * mm]});
            skFitSpline(sketch, "E218", {"points": [v(14.12, 5.64) * mm, v(9.58, 6.13) * mm, v(6.03, 9.63) * mm, v(4.57, 13.8) * mm]});
            skFitSpline(sketch, "E219", {"points": [v(4.57, 13.8) * mm, v(2.38, 13.97) * mm, v(5.46, 9.4) * mm, v(6.7, 8.22) * mm]});
            skFitSpline(sketch, "E220", {"points": [v(6.7, 8.22) * mm, v(11.23, 3.36) * mm, v(18.4, 4.26) * mm, v(24.43, 4.15) * mm]});
            skFitSpline(sketch, "E221", {"points": [v(24.43, 4.15) * mm, v(27.74, 4.14) * mm, v(31.06, 4.13) * mm, v(34.37, 4.12) * mm]});
            skFitSpline(sketch, "E222", {"points": [v(34.37, 4.12) * mm, v(33.6, 18.14) * mm, v(23.27, 30.97) * mm, v(9.71, 34.68) * mm]});
            skFitSpline(sketch, "E223", {"points": [v(9.71, 34.68) * mm, v(-3.65, 38.75) * mm, v(-19.1, 33.5) * mm, v(-27.3, 22.22) * mm]});
            skFitSpline(sketch, "E224", {"points": [v(-27.3, 22.22) * mm, v(-31.72, 16.35) * mm, v(-34.08, 9.03) * mm, v(-34.1, 1.69) * mm]});
            skFitSpline(sketch, "E225", {"points": [v(-34.1, 1.69) * mm, v(-32.97, 1.6) * mm, v(-32.88, 1.6) * mm, v(-32.96, 2.83) * mm]});
            skFitSpline(sketch, "E226", {"points": [v(-21.86, 1.72) * mm, v(-22.19, 3.52) * mm, v(-24.24, 2.5) * mm, v(-25.51, 2.77) * mm]});
            skFitSpline(sketch, "E227", {"points": [v(-25.51, 2.77) * mm, v(-27.6, 2.77) * mm, v(-29.67, 2.77) * mm, v(-31.75, 2.77) * mm]});
            skFitSpline(sketch, "E228", {"points": [v(-31.75, 2.77) * mm, v(-31.53, 16.11) * mm, v(-21.97, 28.6) * mm, v(-9.15, 32.31) * mm]});
            skFitSpline(sketch, "E229", {"points": [v(-9.15, 32.31) * mm, v(2.9, 36.15) * mm, v(16.98, 31.92) * mm, v(24.88, 22.03) * mm]});
            skFitSpline(sketch, "E230", {"points": [v(24.88, 22.03) * mm, v(28.79, 17.3) * mm, v(31.26, 11.43) * mm, v(31.95, 5.35) * mm]});
            skFitSpline(sketch, "E231", {"points": [v(31.95, 5.35) * mm, v(34.66, 5.13) * mm, v(31.65, 9.9) * mm, v(31.78, 11.46) * mm]});
            skFitSpline(sketch, "E232", {"points": [v(31.78, 11.46) * mm, v(27.88, 24.86) * mm, v(14.7, 34.77) * mm, v(0.75, 34.79) * mm]});
            skFitSpline(sketch, "E233", {"points": [v(0.75, 34.79) * mm, v(-13.14, 35.24) * mm, v(-26.6, 25.85) * mm, v(-31, 12.68) * mm]});
            skFitSpline(sketch, "E234", {"points": [v(-31, 12.68) * mm, v(-32.26, 9.16) * mm, v(-32.83, 5.42) * mm, v(-32.89, 1.69) * mm]});
            skFitSpline(sketch, "E235", {"points": [v(-32.89, 1.69) * mm, v(-29.21, 1.7) * mm, v(-25.54, 1.66) * mm, v(-21.86, 1.72) * mm]});
            skFitSpline(sketch, "E236", {"points": [v(-12.76, 2.23) * mm, v(-7.2, 3.03) * mm, v(-2.72, 7.32) * mm, v(-0.9, 12.52) * mm]});
            skFitSpline(sketch, "E237", {"points": [v(-0.9, 12.52) * mm, v(0.85, 17.27) * mm, v(5.1, 22.04) * mm, v(10.63, 21.25) * mm]});
            skFitSpline(sketch, "E238", {"points": [v(10.63, 21.25) * mm, v(17.75, 20.41) * mm, v(23.15, 12.04) * mm, v(19.97, 5.35) * mm]});
            skFitSpline(sketch, "E239", {"points": [v(19.97, 5.35) * mm, v(22.99, 5.32) * mm, v(21.88, 10.6) * mm, v(21.6, 12.64) * mm]});
            skFitSpline(sketch, "E240", {"points": [v(21.6, 12.64) * mm, v(19.88, 19.73) * mm, v(11.06, 25.07) * mm, v(4.37, 21) * mm]});
            skFitSpline(sketch, "E241", {"points": [v(4.37, 21) * mm, v(-0.05, 18.57) * mm, v(-1.37, 13.5) * mm, v(-3.7, 9.43) * mm]});
            skFitSpline(sketch, "E242", {"points": [v(-3.7, 9.43) * mm, v(-5.87, 5.8) * mm, v(-9.86, 3.6) * mm, v(-14, 3.12) * mm]});
            skFitSpline(sketch, "E243", {"points": [v(-14, 3.12) * mm, v(-13.63, 2.79) * mm, v(-13.57, 1.59) * mm, v(-12.76, 2.23) * mm]});
            skFitSpline(sketch, "E244", {"points": [v(-22.5, 2.95) * mm, v(-22.8, 4.75) * mm, v(-24.88, 3.72) * mm, v(-26.12, 3.99) * mm]});
            skFitSpline(sketch, "E245", {"points": [v(-26.12, 3.99) * mm, v(-28.63, 3.82) * mm, v(-31.68, 3.4) * mm, v(-30.13, 6.83) * mm]});
            skFitSpline(sketch, "E246", {"points": [v(-30.13, 6.83) * mm, v(-28.14, 20.06) * mm, v(-16.56, 31) * mm, v(-3.26, 32.3) * mm]});
            skFitSpline(sketch, "E247", {"points": [v(-3.26, 32.3) * mm, v(9.33, 33.88) * mm, v(22.37, 26.74) * mm, v(27.8, 15.27) * mm]});
            skFitSpline(sketch, "E248", {"points": [v(27.8, 15.27) * mm, v(29.94, 12.49) * mm, v(29.45, 7.28) * mm, v(31.47, 5.35) * mm]});
            skFitSpline(sketch, "E249", {"points": [v(31.47, 5.35) * mm, v(32, 8.65) * mm, v(29.89, 13.5) * mm, v(28.18, 16.9) * mm]});
            skFitSpline(sketch, "E250", {"points": [v(28.18, 16.9) * mm, v(22.1, 28.5) * mm, v(8.4, 35.35) * mm, v(-4.52, 33.23) * mm]});
            skFitSpline(sketch, "E251", {"points": [v(-4.52, 33.23) * mm, v(-17.94, 31.42) * mm, v(-29.34, 20.15) * mm, v(-31.25, 6.74) * mm]});
            skFitSpline(sketch, "E252", {"points": [v(-31.25, 6.74) * mm, v(-31.79, 4.53) * mm, v(-32.24, 2.08) * mm, v(-29.33, 2.9) * mm]});
            skFitSpline(sketch, "E253", {"points": [v(-29.33, 2.9) * mm, v(-27.06, 2.92) * mm, v(-24.78, 2.87) * mm, v(-22.5, 2.95) * mm]});
            skFitSpline(sketch, "E254", {"points": [v(-13.4, 3.35) * mm, v(-7.91, 3.98) * mm, v(-3.57, 8.25) * mm, v(-1.87, 13.36) * mm]});
            skFitSpline(sketch, "E255", {"points": [v(-1.87, 13.36) * mm, v(0.04, 18.46) * mm, v(4.9, 23.31) * mm, v(10.75, 22.46) * mm]});
            skFitSpline(sketch, "E256", {"points": [v(10.75, 22.46) * mm, v(18.47, 21.6) * mm, v(24.35, 12.74) * mm, v(21.32, 5.38) * mm]});
            skFitSpline(sketch, "E257", {"points": [v(21.32, 5.38) * mm, v(24.26, 5.4) * mm, v(23.05, 10.7) * mm, v(22.84, 12.75) * mm]});
            skFitSpline(sketch, "E258", {"points": [v(22.84, 12.75) * mm, v(21.1, 20.22) * mm, v(12.31, 26) * mm, v(4.93, 22.67) * mm]});
            skFitSpline(sketch, "E259", {"points": [v(4.93, 22.67) * mm, v(0.1, 20.6) * mm, v(-2.18, 15.58) * mm, v(-4.14, 11.05) * mm]});
            skFitSpline(sketch, "E260", {"points": [v(-4.14, 11.05) * mm, v(-6.1, 7.02) * mm, v(-10.32, 4.63) * mm, v(-14.68, 4.25) * mm]});
            skFitSpline(sketch, "E261", {"points": [v(-14.68, 4.25) * mm, v(-14.34, 3.86) * mm, v(-14.26, 2.68) * mm, v(-13.4, 3.35) * mm]});
            skFitSpline(sketch, "E262", {"points": [v(-23.08, 4.19) * mm, v(-23.29, 6.06) * mm, v(-25.6, 4.87) * mm, v(-26.87, 5.2) * mm]});
            skFitSpline(sketch, "E263", {"points": [v(-26.87, 5.2) * mm, v(-31.3, 4.54) * mm, v(-27.52, 10.82) * mm, v(-27, 13.27) * mm]});
            skFitSpline(sketch, "E264", {"points": [v(-27, 13.27) * mm, v(-22.36, 24.6) * mm, v(-10.16, 32.15) * mm, v(2.04, 31.2) * mm]});
            skFitSpline(sketch, "E265", {"points": [v(2.04, 31.2) * mm, v(15.16, 30.63) * mm, v(26.91, 20.18) * mm, v(29.19, 7.29) * mm]});
            skFitSpline(sketch, "E266", {"points": [v(29.19, 7.29) * mm, v(29.1, 4.22) * mm, v(31.62, 5.25) * mm, v(30.21, 7.72) * mm]});
            skFitSpline(sketch, "E267", {"points": [v(30.21, 7.72) * mm, v(27.86, 20.53) * mm, v(16.5, 30.99) * mm, v(3.5, 32.18) * mm]});
            skFitSpline(sketch, "E268", {"points": [v(3.5, 32.18) * mm, v(-9.67, 33.83) * mm, v(-23.23, 25.76) * mm, v(-28.11, 13.43) * mm]});
            skFitSpline(sketch, "E269", {"points": [v(-28.11, 13.43) * mm, v(-28.86, 10.8) * mm, v(-31.2, 5.93) * mm, v(-29.72, 4.13) * mm]});
            skFitSpline(sketch, "E270", {"points": [v(-29.72, 4.13) * mm, v(-27.5, 4.15) * mm, v(-25.3, 4.07) * mm, v(-23.08, 4.19) * mm]});
            skFitSpline(sketch, "E271", {"points": [v(-13.83, 4.52) * mm, v(-8.82, 5.01) * mm, v(-4.73, 8.8) * mm, v(-3.15, 13.47) * mm]});
            skFitSpline(sketch, "E272", {"points": [v(-3.15, 13.47) * mm, v(-1.1, 19.02) * mm, v(3.94, 24.3) * mm, v(10.3, 23.73) * mm]});
            skFitSpline(sketch, "E273", {"points": [v(10.3, 23.73) * mm, v(18.88, 23.2) * mm, v(25.7, 13.56) * mm, v(22.6, 5.35) * mm]});
            skFitSpline(sketch, "E274", {"points": [v(22.6, 5.35) * mm, v(25.18, 5.05) * mm, v(24.13, 9.42) * mm, v(24.36, 11.04) * mm]});
            skFitSpline(sketch, "E275", {"points": [v(24.36, 11.04) * mm, v(23.64, 19.92) * mm, v(13.7, 27.4) * mm, v(5.06, 24.04) * mm]});
            skFitSpline(sketch, "E276", {"points": [v(5.06, 24.04) * mm, v(-0.17, 22.1) * mm, v(-3.06, 16.91) * mm, v(-5.02, 12.02) * mm]});
            skFitSpline(sketch, "E277", {"points": [v(-5.02, 12.02) * mm, v(-6.8, 7.96) * mm, v(-11.06, 5.62) * mm, v(-15.37, 5.42) * mm]});
            skFitSpline(sketch, "E278", {"points": [v(-15.37, 5.42) * mm, v(-15.1, 4.61) * mm, v(-14.7, 4.15) * mm, v(-13.83, 4.52) * mm]});
            skFitSpline(sketch, "E279", {"points": [v(-23.55, 5.43) * mm, v(-26.77, 14.95) * mm, v(-17.97, 25.83) * mm, v(-8.04, 24.94) * mm]});
            skFitSpline(sketch, "E280", {"points": [v(-8.04, 24.94) * mm, v(-4.77, 25.21) * mm, v(-1.78, 22.05) * mm, v(0.49, 21.27) * mm]});
            skFitSpline(sketch, "E281", {"points": [v(0.49, 21.27) * mm, v(5.1, 26.03) * mm, v(13.08, 26.06) * mm, v(18.13, 21.99) * mm]});
            skFitSpline(sketch, "E282", {"points": [v(18.13, 21.99) * mm, v(23.17, 18.32) * mm, v(25.92, 11.47) * mm, v(23.92, 5.43) * mm]});
            skFitSpline(sketch, "E283", {"points": [v(23.92, 5.43) * mm, v(26.5, 5.37) * mm, v(31.08, 4.33) * mm, v(28.8, 8.48) * mm]});
            skFitSpline(sketch, "E284", {"points": [v(28.8, 8.48) * mm, v(26.05, 21.06) * mm, v(14.18, 30.85) * mm, v(1.3, 31.11) * mm]});
            skFitSpline(sketch, "E285", {"points": [v(1.3, 31.11) * mm, v(-11.9, 31.86) * mm, v(-24.76, 22.47) * mm, v(-28.12, 9.68) * mm]});
            skFitSpline(sketch, "E286", {"points": [v(-28.12, 9.68) * mm, v(-29.5, 6.57) * mm, v(-29.09, 4.42) * mm, v(-25.4, 5.35) * mm]});
            skFitSpline(sketch, "E287", {"points": [v(-25.4, 5.35) * mm, v(-24.79, 5.4) * mm, v(-24.16, 5.26) * mm, v(-23.55, 5.43) * mm]});
            skFitSpline(sketch, "E288", {"points": [v(-14.9, 5.6) * mm, v(-10.36, 5.85) * mm, v(-6.24, 8.8) * mm, v(-4.66, 13.08) * mm]});
            skFitSpline(sketch, "E289", {"points": [v(-4.66, 13.08) * mm, v(-3.15, 17.18) * mm, v(-10.54, 18.88) * mm, v(-13.1, 16.14) * mm]});
            skFitSpline(sketch, "E290", {"points": [v(-13.1, 16.14) * mm, v(-16.51, 13.95) * mm, v(-18.04, 8.73) * mm, v(-15.29, 5.55) * mm]});
            skFitSpline(sketch, "E291", {"points": [v(15.88, 5.68) * mm, v(19.3, 10.42) * mm, v(15, 17.46) * mm, v(9.44, 17.52) * mm]});
            skFitSpline(sketch, "E292", {"points": [v(9.44, 17.52) * mm, v(5.52, 17.56) * mm, v(3.07, 13.54) * mm, v(6.33, 10.66) * mm]});
            skFitSpline(sketch, "E293", {"points": [v(6.33, 10.66) * mm, v(8.29, 7.44) * mm, v(12.27, 5.58) * mm, v(15.88, 5.68) * mm]});
            skLineSegment(sketch, "E294", {"start": v(-15.29, 5.55) * mm, "end": v(-14.9, 5.6) * mm});
            skLineSegment(sketch, "E295", {"start": v(-14.9, 5.6) * mm, "end": v(-15.29, 5.55) * mm});
            skSolve(sketch);
        }
        {
            var Q0;
            Q0=makeQuery(id+"F6.imprint","IMPRINT",FACE,{"disambiguationData":[TD([[makeQuery(id+"F6.imprint","IMPRINT",EDGE,{"derivedFrom":sQuery(id+"F6.wireOp",EDGE,"E187")}),1.0]])]});
            var Q1;
            Q1=makeQuery(id+"F6.imprint","IMPRINT",FACE,{"disambiguationData":[TD([[makeQuery(id+"F6.imprint","IMPRINT",EDGE,{"derivedFrom":sQuery(id+"F6.wireOp",EDGE,"E214")}),1.0]])]});
            var Q2;
            Q2=makeQuery(id+"F6.imprint","IMPRINT",FACE,{"disambiguationData":[TD([[makeQuery(id+"F6.imprint","IMPRINT",EDGE,{"derivedFrom":sQuery(id+"F6.wireOp",EDGE,"E244")}),1.0]])]});
            var Q3;
            Q3=makeQuery(id+"F6.imprint","IMPRINT",FACE,{"disambiguationData":[TD([[makeQuery(id+"F6.imprint","IMPRINT",EDGE,{"derivedFrom":sQuery(id+"F6.wireOp",EDGE,"E93")}),1.0]])]});
            var Q4;
            {var subQ8=sQuery(id+"F6.wireOp",EDGE,"E116");Q4=makeQuery(id+"F6.imprint","IMPRINT",FACE,{"disambiguationData":[TD([[makeQuery(id+"F6.imprint","IMPRINT",EDGE,{"derivedFrom":subQ8}),1.0]])]});}
            var Q5;
            {var subQ1=sQuery(id+"F6.wireOp",EDGE,"E135");Q5=makeQuery(id+"F6.imprint","IMPRINT",FACE,{"disambiguationData":[TD([[makeQuery(id+"F6.imprint","IMPRINT",EDGE,{"derivedFrom":subQ1}),1.0]])]});}
            var Q6;
            {var subQ7=sQuery(id+"F6.wireOp",EDGE,"E50");Q6=makeQuery(id+"F6.imprint","IMPRINT",FACE,{"disambiguationData":[TD([[makeQuery(id+"F6.imprint","IMPRINT",EDGE,{"derivedFrom":subQ7}),1.0]])]});}
            var Q7;
            Q7=makeQuery(id+"F6.imprint","IMPRINT",FACE,{"disambiguationData":[TD([[makeQuery(id+"F6.imprint","IMPRINT",EDGE,{"derivedFrom":sQuery(id+"F6.wireOp",EDGE,"E74")}),1.0]])]});
            var Q8;
            {var subQ7=sQuery(id+"F6.wireOp",EDGE,"E28");Q8=makeQuery(id+"F6.imprint","IMPRINT",FACE,{"disambiguationData":[TD([[makeQuery(id+"F6.imprint","IMPRINT",EDGE,{"derivedFrom":subQ7}),1.0]])]});}
            var Q9;
            Q9=makeQuery(id+"F6.imprint","IMPRINT",FACE,{"disambiguationData":[TD([[makeQuery(id+"F6.imprint","IMPRINT",EDGE,{"derivedFrom":sQuery(id+"F6.wireOp",EDGE,"E271")}),1.0]])]});
            var Q10;
            {var subQ13=sQuery(id+"F6.wireOp",EDGE,"E237");Q10=makeQuery(id+"F6.imprint","IMPRINT",FACE,{"disambiguationData":[TD([[makeQuery(id+"F6.imprint","IMPRINT",EDGE,{"derivedFrom":subQ13}),1.0]])]});}
            var Q11;
            {var subQ0=sQuery(id+"F6.wireOp",EDGE,"E170");Q11=makeQuery(id+"F6.imprint","IMPRINT",FACE,{"disambiguationData":[TD([[makeQuery(id+"F6.imprint","IMPRINT",EDGE,{"derivedFrom":subQ0}),1.0]])]});}
            extrude(context, id + "F7", {"entities" : qUnion([Q0, Q1, Q2, Q3, Q4, Q5, Q6, Q7, Q8, Q9, Q10, Q11]), "operationType" : NewBodyOperationType.REMOVE, "oppositeDirection" : true, "depth" : 4.7 * mm, "offsetDistance" : 25 * mm});
        }
        {
            var Q0;
            Q0=makeQuery(id+"F1.opExtrude","CAP_FACE",FACE,{"disambiguationData":[OSD([sQuery(id+"F0.wireOp",EDGE,"E0.bottom"),sQuery(id+"F0.wireOp",EDGE,"E0.top"),sQuery(id+"F0.wireOp",EDGE,"E0.left"),sQuery(id+"F0.wireOp",EDGE,"E0.right")])],"isStart":false});
            var sketch = newSketch(context, id + "F8", { "sketchPlane" : qUnion([Q0])});
            skLineSegment(sketch, "E296.bottom", {"start": v(-42, -36.8) * mm, "end": v(-30, -36.8) * mm});
            skLineSegment(sketch, "E296.top", {"start": v(-42, -44.8) * mm, "end": v(-30, -44.8) * mm});
            skLineSegment(sketch, "E296.left", {"start": v(-42, -36.8) * mm, "end": v(-42, -44.8) * mm});
            skLineSegment(sketch, "E296.right", {"start": v(-30, -36.8) * mm, "end": v(-30, -44.8) * mm});
            skSolve(sketch);
        }
        {
            var Q0;
            Q0 = qSketchRegion(id + "F8", true);
            extrude(context, id + "F9", {"entities" : qUnion([Q0]), "operationType" : NewBodyOperationType.REMOVE, "oppositeDirection" : true, "depth" : 5 * mm, "offsetDistance" : 25 * mm});
        }
        {
            var Q0;
            Q0=makeQuery(id+"F9.boolean.opBoolean","COPY",EDGE,{"derivedFrom":makeQuery(id+"F9.opExtrude","SWEPT_EDGE",EDGE,{"disambiguationData":[OSD([sQuery(id+"F8.wireOp",EDGE,"E296.bottom"),sQuery(id+"F8.wireOp",EDGE,"E296.left")])]})});
            var Q1;
            Q1=makeQuery(id+"F9.boolean.opBoolean","COPY",EDGE,{"derivedFrom":makeQuery(id+"F9.opExtrude","SWEPT_EDGE",EDGE,{"disambiguationData":[OSD([sQuery(id+"F8.wireOp",EDGE,"E296.bottom"),sQuery(id+"F8.wireOp",EDGE,"E296.right")])]})});
            var Q2;
            Q2=makeQuery(id+"F9.boolean.opBoolean","COPY",EDGE,{"derivedFrom":makeQuery(id+"F9.opExtrude","SWEPT_EDGE",EDGE,{"disambiguationData":[OSD([sQuery(id+"F8.wireOp",EDGE,"E296.top"),sQuery(id+"F8.wireOp",EDGE,"E296.left")])]})});
            var Q3;
            Q3=makeQuery(id+"F9.boolean.opBoolean","COPY",EDGE,{"derivedFrom":makeQuery(id+"F9.opExtrude","SWEPT_EDGE",EDGE,{"disambiguationData":[OSD([sQuery(id+"F8.wireOp",EDGE,"E296.top"),sQuery(id+"F8.wireOp",EDGE,"E296.right")])]})});
            fillet(context, id + "F10", {"entities" : qUnion([Q0, Q1, Q2, Q3]), "radius" : 1 * mm, "tangentPropagation" : true, "allowEdgeOverflow" : false});
        }
    });
